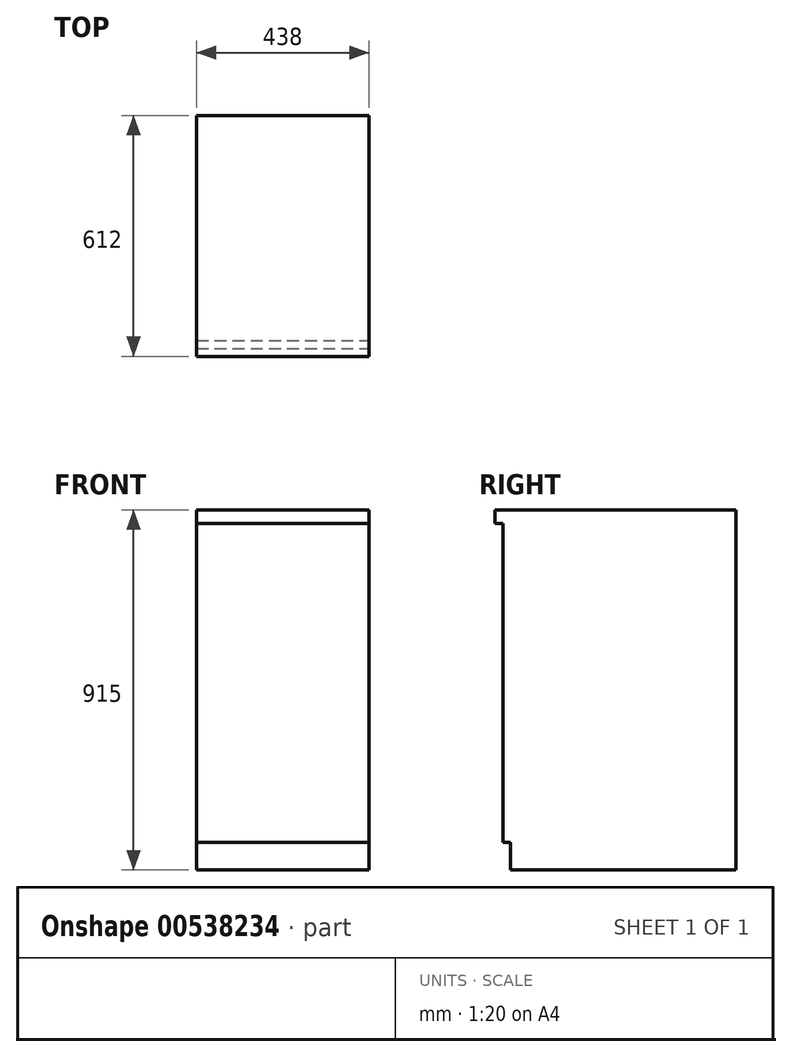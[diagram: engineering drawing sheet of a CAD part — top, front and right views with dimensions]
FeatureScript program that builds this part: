
annotation { "Feature Type Name" : "Feature", "Feature Type Description" : "" }
export const myFeature = defineFeature(function(context is Context, id is Id, definition is map)
    precondition{}
    {
        {
            var Q0;
            Q0=qCreatedBy(makeId("Top.planeOp"),FACE);
            var sketch = newSketch(context, id + "F0", { "sketchPlane" : qUnion([Q0])});
            skLineSegment(sketch, "E0.bottom", {"start": v(0, 0) * mm, "end": v(-438, 0) * mm});
            skLineSegment(sketch, "E0.top", {"start": v(0, 612) * mm, "end": v(-438, 612) * mm});
            skLineSegment(sketch, "E0.left", {"start": v(0, 0) * mm, "end": v(0, 612) * mm});
            skLineSegment(sketch, "E0.right", {"start": v(-438, 0) * mm, "end": v(-438, 612) * mm});
            skSolve(sketch);
        }
        {
            var Q0;
            Q0 = qSketchRegion(id + "F0", true);
            extrude(context, id + "F1", {"entities" : qUnion([Q0]), "depth" : 915 * mm, "offsetDistance" : 25 * mm});
        }
        {
            var Q0;
            Q0=makeQuery(id+"F1.opExtrude","SWEPT_FACE",FACE,{"disambiguationData":[OSD([sQuery(id+"F0.wireOp",EDGE,"E0.left")])]});
            var sketch = newSketch(context, id + "F2", { "sketchPlane" : qUnion([Q0])});
            skLineSegment(sketch, "E1.bottom", {"start": v(0, 0) * mm, "end": v(20, 0) * mm});
            skLineSegment(sketch, "E1.top", {"start": v(0, 880) * mm, "end": v(20, 880) * mm});
            skLineSegment(sketch, "E1.left", {"start": v(0, 0) * mm, "end": v(0, 880) * mm});
            skLineSegment(sketch, "E1.right", {"start": v(20, 0) * mm, "end": v(20, 880) * mm});
            skSolve(sketch);
        }
        {
            var Q0;
            Q0 = qSketchRegion(id + "F2", true);
            extrude(context, id + "F3", {"entities" : qUnion([Q0]), "operationType" : NewBodyOperationType.REMOVE, "endBound" : BoundingType.THROUGH_ALL, "oppositeDirection" : true, "depth" : 25 * mm, "offsetDistance" : 25 * mm});
        }
        {
            var Q0;
            Q0=makeQuery(id+"F1.opExtrude","SWEPT_FACE",FACE,{"disambiguationData":[OSD([sQuery(id+"F0.wireOp",EDGE,"E0.left")])]});
            var sketch = newSketch(context, id + "F4", { "sketchPlane" : qUnion([Q0])});
            skLineSegment(sketch, "E2.bottom", {"start": v(20, 70) * mm, "end": v(40, 70) * mm});
            skLineSegment(sketch, "E2.top", {"start": v(20, 0) * mm, "end": v(40, 0) * mm});
            skLineSegment(sketch, "E2.left", {"start": v(20, 70) * mm, "end": v(20, 0) * mm});
            skLineSegment(sketch, "E2.right", {"start": v(40, 70) * mm, "end": v(40, 0) * mm});
            skSolve(sketch);
        }
        {
            var Q0;
            Q0 = qSketchRegion(id + "F4", true);
            extrude(context, id + "F5", {"entities" : qUnion([Q0]), "operationType" : NewBodyOperationType.REMOVE, "endBound" : BoundingType.THROUGH_ALL, "oppositeDirection" : true, "depth" : 25 * mm, "offsetDistance" : 25 * mm});
        }
    });
